# Revit family: Kurpie Chair Lantana
name_source: partatom
category: Furniture
units: mm (PartAtom-declared; Revit-internal decimal feet)

## family parameters
Always vertical = Yes
Cut with Voids When Loaded = No
Enable Cutting in Views = No
OmniClass Number = 23.40.20.00
OmniClass Title = General Furniture and Specialties
Render Appearance Source = Family Geometry
Room Calculation Point = No
Shared = No
Work Plane-Based = No

## types (4) — shared parameters
Cost = 1 $
Default Elevation = 0' - 0"
Depth = 1' - 6 1/8"
ES Seat Count = 1
HS Seat Count = 1
Height = 2' - 9 21/32"
Seat Height = 1' - 5 23/32"
Stack Height = 8
UK Primary Seat Count = 1
UK Secondary Seat Count = 1
Width = 1' - 7 11/16"

## per-type parameters (varying)
| type | Model |
| Laminate, 4 leg | KU-STL-T01-90942 |
| Laminate, sled | KU-STS-T01-90942 |
| Stain, 4 leg | KU-STL-T01-1.043 |
| Stain, sled | KU-STS-T01-1.043 |

## geometry (parser evidence)
native form markers: Sweep x3
no freeform markers — native parametric forms only
